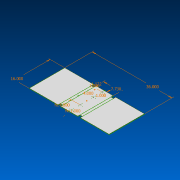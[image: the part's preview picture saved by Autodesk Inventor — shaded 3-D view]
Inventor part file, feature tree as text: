
AUTODESK INVENTOR PART (.ipt)
format: ipt  version: 2022 (Build 260153000, 153)  size: 111,616 bytes
history: native  units: in
note: dims shown in document units (in); Inventor stores cm internally (conversion verified against a paired STEP export)
features: sketch x1, extrude x1, hole x1
ambient origin geometry x8: Origin, YZ Plane, XZ Plane, XY Plane, X Axis, Y Axis, Z Axis, Center Point
bodies: Solid1 (feature_tree)
feature tree (3):
  sketch  "Sketch1"  dims[d0=1.0in d1=1.1216in d3=7.7295in d4=16.0in d5=36.0in d8=4.0in d9=4.0in d10=1.0in d11=1.0in d12=0.064in d13=0.0in d14=0.18in d15=0.75in d16=0.375in d17=0.25in d18=0.5635in d19=1.0in d20=0.0in]
  extrude  "Extrusion1"  Depth=1.1216in
  hole  "Hole1"  [1 undecoded]
note: 1 required parameter value undecoded (feature->parameter linkage not recoverable at this tier; creation-order binding heuristic only, values carry confidence <= 0.55)
